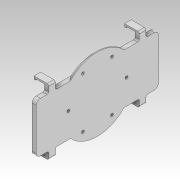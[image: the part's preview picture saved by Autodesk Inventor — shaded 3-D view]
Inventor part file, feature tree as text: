
AUTODESK INVENTOR PART (.ipt)
format: ipt  version: 2020 (Build 240168000, 168)  size: 248,320 bytes
history: native  units: mm
features: sketch x6, extrude x5, fillet x3, projected_geometry x2, revolve x1, plane x1, pattern_circular x1
ambient origin geometry x8: Origin, YZ Plane, XZ Plane, XY Plane, X Axis, Y Axis, Z Axis, Center Point
bodies: Solid1 (feature_tree)
feature tree (19):
  revolve  "Revolution1"  [1 undecoded]
  extrude  "Extrusion1"  Depth=3.3mm
  plane  "Work Plane1"
  extrude  "Extrusion2"  TaperAngle=0.0deg  [1 undecoded]
  pattern_circular  "Circular Pattern1"  Count=6 Angle=360.0deg
  extrude  "Extrusion3"  Depth=2.0mm
  extrude  "Extrusion4"  TaperAngle=45.0deg  [1 undecoded]
  extrude  "Extrusion5"  Depth=2.0mm
  fillet  "Fillet1"  Radius=60.0mm
  fillet  "Fillet2"  Radius=15.0mm
  fillet  "Fillet3"  Radius=8.0mm
  sketch  "Sketch1"  dims[d0=44.0mm d3=1.0mm]
  sketch  "Sketch2"  dims[d6=90.0deg d7=3.3mm]
  sketch  "Sketch3"  dims[d8=35.0mm d9=0.0mm d10=0.0mm]
  sketch  "Sketch4"  dims[d11=-2.0mm]
  sketch  "Sketch5"  dims[d12=6.0mm]
  sketch  "Sketch6"  dims[d13=2.0mm d14=0.0mm d15=60.0mm d16=360.0deg d19=5.0mm d20=45.0deg d21=147.0mm d22=60.0mm d23=15.0mm d24=8.0mm d26=15.0mm d27=10.0mm d28=0.0mm d29=75.0mm d30=2.0mm d31=10.6mm d32=2.0mm d33=1.5mm d34=10.0mm d35=0.0mm d36=10.0mm d37=0.0mm d38=5.0mm d39=2.0mm d40=2.0mm]
  projected_geometry  "Projected Loop1"
  projected_geometry  "Projected Loop2"
note: 3 required parameter values undecoded (feature->parameter linkage not recoverable at this tier; creation-order binding heuristic only, values carry confidence <= 0.55)